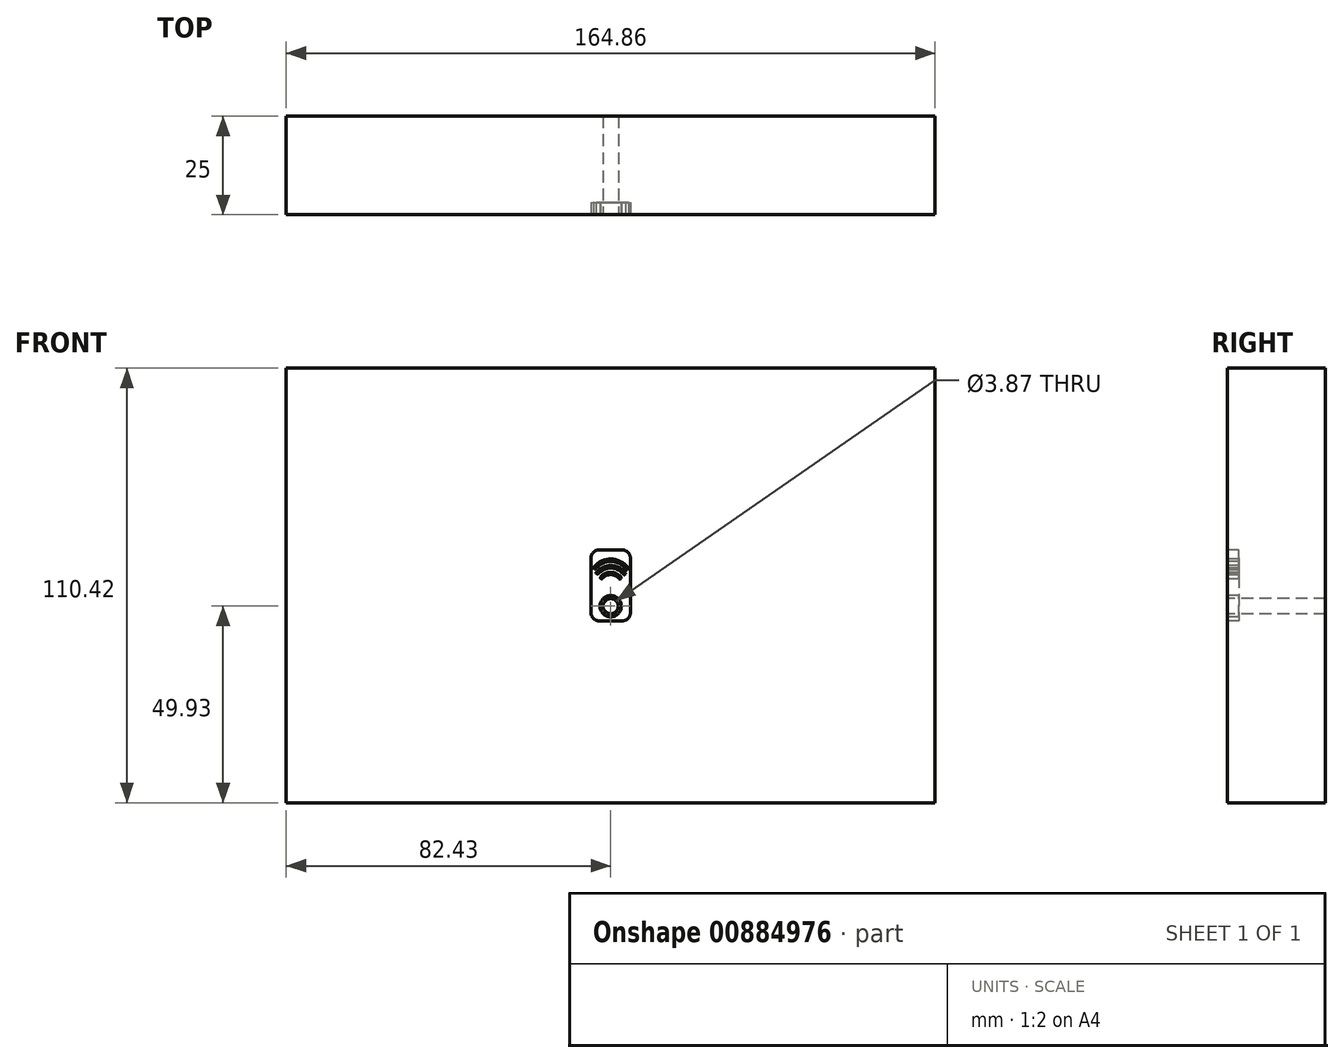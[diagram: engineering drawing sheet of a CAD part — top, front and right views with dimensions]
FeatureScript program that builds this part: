
annotation { "Feature Type Name" : "Feature", "Feature Type Description" : "" }
export const myFeature = defineFeature(function(context is Context, id is Id, definition is map)
    precondition{}
    {
        {
            var Q0;
            Q0=qCreatedBy(makeId("Front.planeOp"),FACE);
            var sketch = newSketch(context, id + "F0", { "sketchPlane" : qUnion([Q0])});
            skLineSegment(sketch, "E0.bottom", {"start": v(-82.43, 55.21) * mm, "end": v(82.43, 55.21) * mm});
            skLineSegment(sketch, "E0.top", {"start": v(-82.43, -55.21) * mm, "end": v(82.43, -55.21) * mm});
            skLineSegment(sketch, "E0.left", {"start": v(-82.43, 55.21) * mm, "end": v(-82.43, -55.21) * mm});
            skLineSegment(sketch, "E0.right", {"start": v(82.43, 55.21) * mm, "end": v(82.43, -55.21) * mm});
            skPoint(sketch, "E0.middle", {"position": v(0, 0) * mm});
            skSolve(sketch);
        }
        {
            var Q0;
            Q0 = qSketchRegion(id + "F0", true);
            extrude(context, id + "F1", {"entities" : qUnion([Q0]), "depth" : 25 * mm, "offsetDistance" : 25 * mm});
        }
        {
            var Q0;
            Q0=makeQuery(id+"F1.opExtrude","CAP_FACE",FACE,{"disambiguationData":[OSD([sQuery(id+"F0.wireOp",EDGE,"E0.bottom"),sQuery(id+"F0.wireOp",EDGE,"E0.top"),sQuery(id+"F0.wireOp",EDGE,"E0.left"),sQuery(id+"F0.wireOp",EDGE,"E0.right")])],"isStart":false});
            var sketch = newSketch(context, id + "F2", { "sketchPlane" : qUnion([Q0])});
            skLineSegment(sketch, "E1.bottom", {"start": v(-5, 9) * mm, "end": v(5, 9) * mm});
            skLineSegment(sketch, "E1.top", {"start": v(-5, -9) * mm, "end": v(5, -9) * mm});
            skLineSegment(sketch, "E1.left", {"start": v(-5, 9) * mm, "end": v(-5, -9) * mm});
            skLineSegment(sketch, "E1.right", {"start": v(5, 9) * mm, "end": v(5, -9) * mm});
            skPoint(sketch, "E1.middle", {"position": v(0, 0) * mm});
            skArc(sketch, "E2", {"start": v(-2.23, 1.6) * mm, "mid": v(0.02, 2.74) * mm, "end": v(2.26, 1.55) * mm});
            skLineSegment(sketch, "E3", {"start": v(0, 0) * mm, "end": v(2.26, 1.55) * mm, "construction": true});
            skLineSegment(sketch, "E4", {"start": v(0, 0) * mm, "end": v(-2.23, 1.6) * mm, "construction": true});
            skArc(sketch, "E5.0", {"start": v(-2.72, 1.94) * mm, "mid": v(0.03, 3.34) * mm, "end": v(2.75, 1.9) * mm});
            skLineSegment(sketch, "E6", {"start": v(2.26, 1.55) * mm, "end": v(2.75, 1.9) * mm});
            skLineSegment(sketch, "E7", {"start": v(-2.72, 1.94) * mm, "end": v(-2.23, 1.6) * mm});
            skArc(sketch, "E8", {"start": v(-3.27, 2.78) * mm, "mid": v(0.1, 4.43) * mm, "end": v(3.38, 2.62) * mm});
            skLineSegment(sketch, "E9", {"start": v(0, 0.37) * mm, "end": v(3.38, 2.62) * mm, "construction": true});
            skLineSegment(sketch, "E10", {"start": v(0, 0.37) * mm, "end": v(-3.27, 2.78) * mm, "construction": true});
            skArc(sketch, "E11.0", {"start": v(-3.76, 3.13) * mm, "mid": v(0.1, 5.03) * mm, "end": v(3.88, 2.96) * mm});
            skLineSegment(sketch, "E12", {"start": v(3.38, 2.62) * mm, "end": v(3.88, 2.96) * mm});
            skLineSegment(sketch, "E13", {"start": v(-3.76, 3.13) * mm, "end": v(-3.27, 2.78) * mm});
            skArc(sketch, "E14", {"start": v(-3.92, 4.1) * mm, "mid": v(0.11, 6.08) * mm, "end": v(4.05, 3.9) * mm});
            skLineSegment(sketch, "E15", {"start": v(0, 1.2) * mm, "end": v(4.05, 3.9) * mm, "construction": true});
            skLineSegment(sketch, "E16", {"start": v(0, 1.2) * mm, "end": v(-3.92, 4.1) * mm, "construction": true});
            skArc(sketch, "E17.0", {"start": v(-4.4, 4.45) * mm, "mid": v(0.13, 6.68) * mm, "end": v(4.55, 4.24) * mm});
            skLineSegment(sketch, "E18", {"start": v(4.05, 3.9) * mm, "end": v(4.55, 4.24) * mm});
            skLineSegment(sketch, "E19", {"start": v(-4.4, 4.45) * mm, "end": v(-3.92, 4.1) * mm});
            skCircle(sketch, "E20", {"center": v(0, -5.28) * mm, "radius": 1.93 * mm});
            skCircle(sketch, "E21", {"center": v(0, -5.28) * mm, "radius": 2.7 * mm});
            skSolve(sketch);
        }
        {
            var Q0;
            Q0=makeQuery(id+"F2.imprint","IMPRINT",FACE,{"disambiguationData":[TD([[makeQuery(id+"F2.imprint","IMPRINT",EDGE,{"derivedFrom":sQuery(id+"F2.wireOp",EDGE,"E1.bottom")}),-1.0]])]});
            var Q1;
            Q1=makeQuery(id+"F2.imprint","IMPRINT",FACE,{"disambiguationData":[TD([[makeQuery(id+"F2.imprint","IMPRINT",EDGE,{"derivedFrom":sQuery(id+"F2.wireOp",EDGE,"E20")}),1.0]])]});
            extrude(context, id + "F3", {"entities" : qUnion([Q0, Q1]), "operationType" : NewBodyOperationType.REMOVE, "oppositeDirection" : true, "depth" : 3 * mm, "offsetDistance" : 25 * mm});
        }
        {
            var Q0;
            Q0=makeQuery(id+"F3.boolean.opBoolean","COPY",FACE,{"derivedFrom":makeQuery(id+"F3.opExtrude","CAP_FACE",FACE,{"disambiguationData":[OSD([sQuery(id+"F2.wireOp",EDGE,"E20")])],"isStart":false})});
            extrude(context, id + "F4", {"entities" : qUnion([Q0]), "operationType" : NewBodyOperationType.REMOVE, "oppositeDirection" : true, "depth" : 25 * mm, "offsetDistance" : 25 * mm});
        }
        {
            var Q0;
            Q0=makeQuery(id+"F3.boolean.opBoolean","COPY",EDGE,{"derivedFrom":makeQuery(id+"F3.opExtrude","SWEPT_EDGE",EDGE,{"disambiguationData":[OSD([sQuery(id+"F2.wireOp",EDGE,"E1.bottom"),sQuery(id+"F2.wireOp",EDGE,"E1.left")])]})});
            var Q1;
            Q1=makeQuery(id+"F3.boolean.opBoolean","COPY",EDGE,{"derivedFrom":makeQuery(id+"F3.opExtrude","SWEPT_EDGE",EDGE,{"disambiguationData":[OSD([sQuery(id+"F2.wireOp",EDGE,"E1.bottom"),sQuery(id+"F2.wireOp",EDGE,"E1.right")])]})});
            var Q2;
            Q2=makeQuery(id+"F3.boolean.opBoolean","COPY",EDGE,{"derivedFrom":makeQuery(id+"F3.opExtrude","SWEPT_EDGE",EDGE,{"disambiguationData":[OSD([sQuery(id+"F2.wireOp",EDGE,"E1.top"),sQuery(id+"F2.wireOp",EDGE,"E1.right")])]})});
            var Q3;
            Q3=makeQuery(id+"F3.boolean.opBoolean","COPY",EDGE,{"derivedFrom":makeQuery(id+"F3.opExtrude","SWEPT_EDGE",EDGE,{"disambiguationData":[OSD([sQuery(id+"F2.wireOp",EDGE,"E1.top"),sQuery(id+"F2.wireOp",EDGE,"E1.left")])]})});
            fillet(context, id + "F5", {"entities" : qUnion([Q0, Q1, Q2, Q3]), "radius" : 2 * mm, "tangentPropagation" : true, "allowEdgeOverflow" : false});
        }
        {
            var Q0;
            Q0=makeQuery(id+"F3.boolean.opBoolean","COPY",EDGE,{"derivedFrom":makeQuery(id+"F3.opExtrude","SWEPT_EDGE",EDGE,{"disambiguationData":[OSD([sQuery(id+"F2.wireOp",EDGE,"E14"),sQuery(id+"F2.wireOp",EDGE,"E19")])]})});
            var Q1;
            Q1=makeQuery(id+"F3.boolean.opBoolean","COPY",EDGE,{"derivedFrom":makeQuery(id+"F3.opExtrude","SWEPT_EDGE",EDGE,{"disambiguationData":[OSD([sQuery(id+"F2.wireOp",EDGE,"E17.0"),sQuery(id+"F2.wireOp",EDGE,"E19")])]})});
            var Q2;
            Q2=makeQuery(id+"F3.boolean.opBoolean","COPY",EDGE,{"derivedFrom":makeQuery(id+"F3.opExtrude","SWEPT_EDGE",EDGE,{"disambiguationData":[OSD([sQuery(id+"F2.wireOp",EDGE,"E11.0"),sQuery(id+"F2.wireOp",EDGE,"E13")])]})});
            var Q3;
            Q3=makeQuery(id+"F3.boolean.opBoolean","COPY",EDGE,{"derivedFrom":makeQuery(id+"F3.opExtrude","SWEPT_EDGE",EDGE,{"disambiguationData":[OSD([sQuery(id+"F2.wireOp",EDGE,"E8"),sQuery(id+"F2.wireOp",EDGE,"E13")])]})});
            var Q4;
            Q4=makeQuery(id+"F3.boolean.opBoolean","COPY",EDGE,{"derivedFrom":makeQuery(id+"F3.opExtrude","SWEPT_EDGE",EDGE,{"disambiguationData":[OSD([sQuery(id+"F2.wireOp",EDGE,"E5.0"),sQuery(id+"F2.wireOp",EDGE,"E7")])]})});
            var Q5;
            Q5=makeQuery(id+"F3.boolean.opBoolean","COPY",EDGE,{"derivedFrom":makeQuery(id+"F3.opExtrude","SWEPT_EDGE",EDGE,{"disambiguationData":[OSD([sQuery(id+"F2.wireOp",EDGE,"E2"),sQuery(id+"F2.wireOp",EDGE,"E7")])]})});
            var Q6;
            Q6=makeQuery(id+"F3.boolean.opBoolean","COPY",EDGE,{"derivedFrom":makeQuery(id+"F3.opExtrude","SWEPT_EDGE",EDGE,{"disambiguationData":[OSD([sQuery(id+"F2.wireOp",EDGE,"E2"),sQuery(id+"F2.wireOp",EDGE,"E6")])]})});
            var Q7;
            Q7=makeQuery(id+"F3.boolean.opBoolean","COPY",EDGE,{"derivedFrom":makeQuery(id+"F3.opExtrude","SWEPT_EDGE",EDGE,{"disambiguationData":[OSD([sQuery(id+"F2.wireOp",EDGE,"E5.0"),sQuery(id+"F2.wireOp",EDGE,"E6")])]})});
            var Q8;
            Q8=makeQuery(id+"F3.boolean.opBoolean","COPY",EDGE,{"derivedFrom":makeQuery(id+"F3.opExtrude","SWEPT_EDGE",EDGE,{"disambiguationData":[OSD([sQuery(id+"F2.wireOp",EDGE,"E8"),sQuery(id+"F2.wireOp",EDGE,"E12")])]})});
            var Q9;
            Q9=makeQuery(id+"F3.boolean.opBoolean","COPY",EDGE,{"derivedFrom":makeQuery(id+"F3.opExtrude","SWEPT_EDGE",EDGE,{"disambiguationData":[OSD([sQuery(id+"F2.wireOp",EDGE,"E11.0"),sQuery(id+"F2.wireOp",EDGE,"E12")])]})});
            var Q10;
            Q10=makeQuery(id+"F3.boolean.opBoolean","COPY",EDGE,{"derivedFrom":makeQuery(id+"F3.opExtrude","SWEPT_EDGE",EDGE,{"disambiguationData":[OSD([sQuery(id+"F2.wireOp",EDGE,"E14"),sQuery(id+"F2.wireOp",EDGE,"E18")])]})});
            var Q11;
            Q11=makeQuery(id+"F3.boolean.opBoolean","SPLIT",FACE,{"disambiguationData":[TD([makeQuery(id+"F3.opExtrude","SWEPT_FACE",FACE,{"disambiguationData":[OSD([sQuery(id+"F2.wireOp",EDGE,"E2")])]})])],"derivedFrom":makeQuery(id+"F1.opExtrude","CAP_FACE",FACE,{"disambiguationData":[OSD([sQuery(id+"F0.wireOp",EDGE,"E0.bottom"),sQuery(id+"F0.wireOp",EDGE,"E0.top"),sQuery(id+"F0.wireOp",EDGE,"E0.left"),sQuery(id+"F0.wireOp",EDGE,"E0.right")])],"isStart":false})});
            var Q12;
            Q12=makeQuery(id+"F3.boolean.opBoolean","SPLIT",FACE,{"disambiguationData":[TD([makeQuery(id+"F3.opExtrude","SWEPT_FACE",FACE,{"disambiguationData":[OSD([sQuery(id+"F2.wireOp",EDGE,"E8")])]})])],"derivedFrom":makeQuery(id+"F1.opExtrude","CAP_FACE",FACE,{"disambiguationData":[OSD([sQuery(id+"F0.wireOp",EDGE,"E0.bottom"),sQuery(id+"F0.wireOp",EDGE,"E0.top"),sQuery(id+"F0.wireOp",EDGE,"E0.left"),sQuery(id+"F0.wireOp",EDGE,"E0.right")])],"isStart":false})});
            var Q13;
            Q13=makeQuery(id+"F3.boolean.opBoolean","SPLIT",FACE,{"disambiguationData":[TD([makeQuery(id+"F3.opExtrude","SWEPT_FACE",FACE,{"disambiguationData":[OSD([sQuery(id+"F2.wireOp",EDGE,"E14")])]})])],"derivedFrom":makeQuery(id+"F1.opExtrude","CAP_FACE",FACE,{"disambiguationData":[OSD([sQuery(id+"F0.wireOp",EDGE,"E0.bottom"),sQuery(id+"F0.wireOp",EDGE,"E0.top"),sQuery(id+"F0.wireOp",EDGE,"E0.left"),sQuery(id+"F0.wireOp",EDGE,"E0.right")])],"isStart":false})});
            fillet(context, id + "F6", {"entities" : qUnion([Q0, Q1, Q2, Q3, Q4, Q5, Q6, Q7, Q8, Q9, Q10, Q11, Q12, Q13]), "radius" : 0.2 * mm, "tangentPropagation" : true, "allowEdgeOverflow" : false});
        }
        {
            var Q0;
            Q0=makeQuery(id+"F3.boolean.opBoolean","COPY",EDGE,{"derivedFrom":makeQuery(id+"F3.opExtrude","CAP_EDGE",EDGE,{"disambiguationData":[OSD([sQuery(id+"F2.wireOp",EDGE,"E21")])],"isStart":true})});
            var Q1;
            Q1=makeQuery(id+"F3.boolean.opBoolean","COPY",EDGE,{"derivedFrom":makeQuery(id+"F3.opExtrude","CAP_EDGE",EDGE,{"disambiguationData":[OSD([sQuery(id+"F2.wireOp",EDGE,"E20")])],"isStart":true})});
            fillet(context, id + "F7", {"entities" : qUnion([Q0, Q1]), "radius" : 0.2 * mm, "tangentPropagation" : true, "allowEdgeOverflow" : false});
        }
    });
